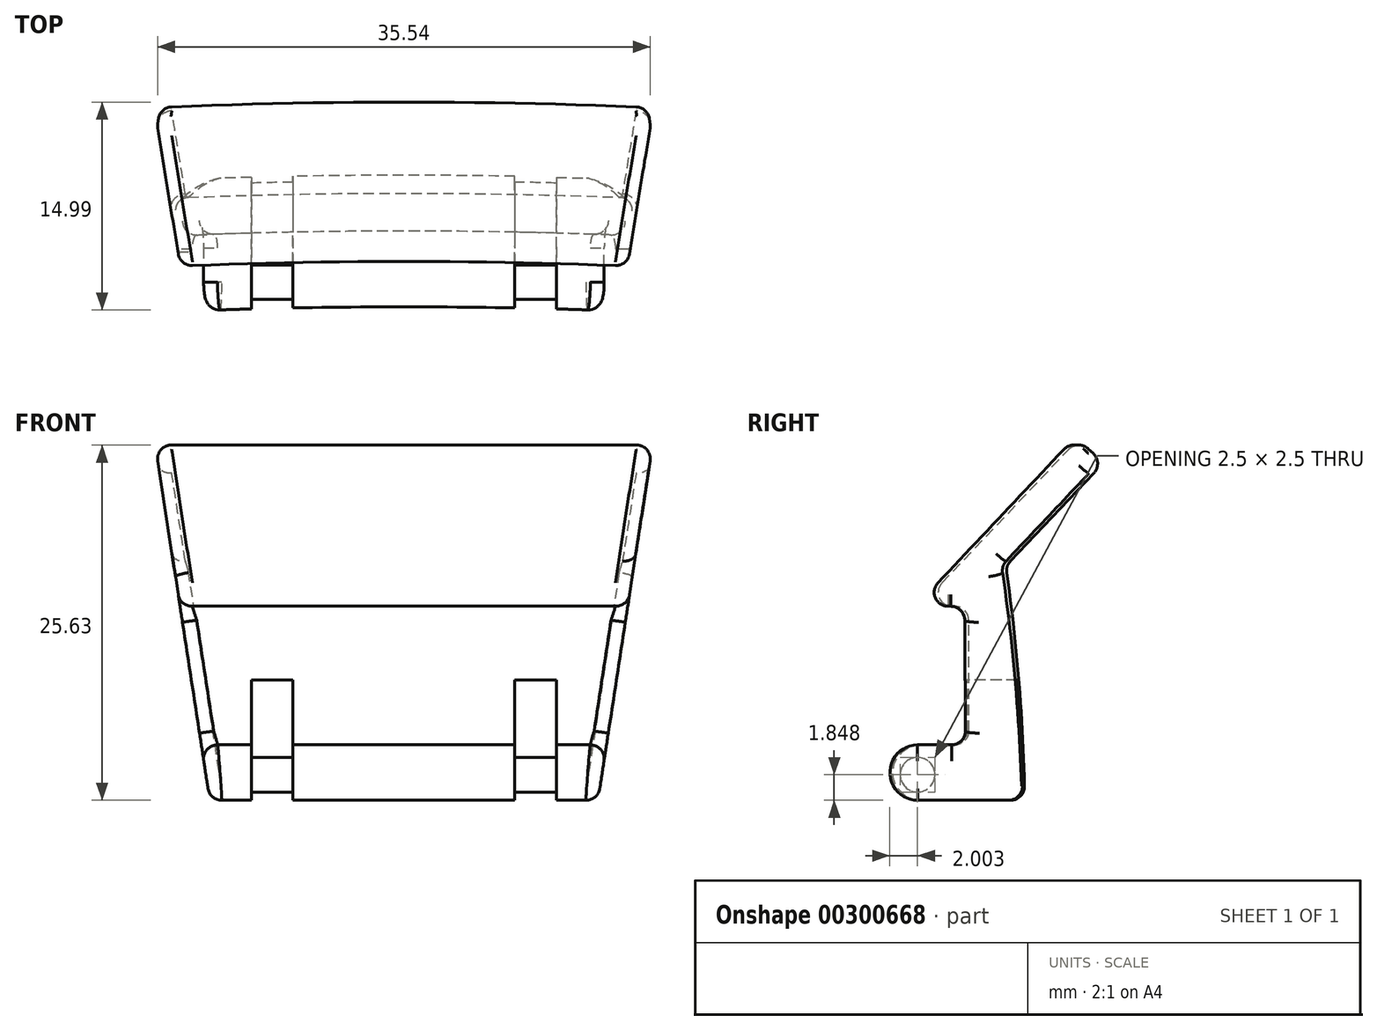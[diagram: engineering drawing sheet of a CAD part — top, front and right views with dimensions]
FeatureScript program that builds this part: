
annotation { "Feature Type Name" : "Feature", "Feature Type Description" : "" }
export const myFeature = defineFeature(function(context is Context, id is Id, definition is map)
    precondition{}
    {
        {
            var Q0;
            Q0=qCreatedBy(makeId("Right.planeOp"),FACE);
            var sketch = newSketch(context, id + "F0", { "sketchPlane" : qUnion([Q0])});
            skLineSegment(sketch, "E0", {"start": v(0, 14) * mm, "end": v(-3.52, 14) * mm});
            skLineSegment(sketch, "E1", {"start": v(-3.52, 14) * mm, "end": v(7.9, 26.05) * mm});
            skArc(sketch, "E2", {"start": v(4.05, 0) * mm, "mid": v(3.63, 8.47) * mm, "end": v(2.68, 16.9) * mm});
            skLineSegment(sketch, "E3", {"start": v(0, 14) * mm, "end": v(0, 4) * mm});
            skLineSegment(sketch, "E4", {"start": v(0, 4) * mm, "end": v(-3.46, 4) * mm});
            skLineSegment(sketch, "E5", {"start": v(-3.46, 0) * mm, "end": v(4.05, 0) * mm});
            skArc(sketch, "E6", {"start": v(-3.46, 4) * mm, "mid": v(-5.46, 2) * mm, "end": v(-3.46, 0) * mm});
            skLineSegment(sketch, "E7", {"start": v(-400, 131.7) * mm, "end": v(-400, -58.06) * mm, "construction": true});
            skPoint(sketch, "E8", {"position": v(2.2, 25.83) * mm});
            skLineSegment(sketch, "E9", {"start": v(7.9, 26.05) * mm, "end": v(9.72, 24.33) * mm});
            skLineSegment(sketch, "E10.trimOffspring", {"start": v(2.68, 16.9) * mm, "end": v(9.72, 24.33) * mm});
            skPoint(sketch, "E11.orphan", {"position": v(2.2, 20.02) * mm});
            skSolve(sketch);
        }
        {
            var Q0;
            Q0 = qSketchRegion(id + "F0", true);
            var Q1;
            Q1=sQuery(id+"F0.wireOp",EDGE,"E7");
            revolve(context, id + "F1", {"entities" : qUnion([Q0]), "axis" : qUnion([Q1]), "revolveType" : RevolveType.SYMMETRIC, "angle" : 10 * degree});
        }
        {
            var Q0;
            Q0=qCreatedBy(makeId("Front.planeOp"),FACE);
            var sketch = newSketch(context, id + "F2", { "sketchPlane" : qUnion([Q0])});
            skLineSegment(sketch, "E12", {"start": v(-14, 0) * mm, "end": v(-18, 26.05) * mm});
            skLineSegment(sketch, "E13", {"start": v(0, -20.72) * mm, "end": v(0, 33) * mm, "construction": true});
            skLineSegment(sketch, "E14", {"start": v(-11, -2.73) * mm, "end": v(-11, 8.67) * mm});
            skLineSegment(sketch, "E15", {"start": v(-11, 8.67) * mm, "end": v(-8, 8.67) * mm});
            skLineSegment(sketch, "E16", {"start": v(-8, 8.67) * mm, "end": v(-8, -4.43) * mm});
            skLineSegment(sketch, "E17", {"start": v(-11, -2.73) * mm, "end": v(-14, 0) * mm});
            skLineSegment(sketch, "E18", {"start": v(-8, -4.43) * mm, "end": v(0, -4.43) * mm});
            skPoint(sketch, "E18.endSnap0", {"position": v(0, 6.14) * mm});
            skLineSegment(sketch, "E19", {"start": v(-18, 26.05) * mm, "end": v(-24.18, 31.48) * mm});
            skLineSegment(sketch, "E20", {"start": v(-24.18, 31.48) * mm, "end": v(-48.84, 27.93) * mm});
            skLineSegment(sketch, "E21", {"start": v(-48.84, 27.93) * mm, "end": v(-46.83, -19.22) * mm});
            skLineSegment(sketch, "E22", {"start": v(-46.83, -19.22) * mm, "end": v(0, -26.62) * mm});
            skLineSegment(sketch, "E23.MirrorCS", {"start": v(46.83, -19.22) * mm, "end": v(0, -26.62) * mm});
            skLineSegment(sketch, "E24.MirrorCS", {"start": v(48.84, 27.93) * mm, "end": v(46.83, -19.22) * mm});
            skLineSegment(sketch, "E25.MirrorCS", {"start": v(24.18, 31.48) * mm, "end": v(48.84, 27.93) * mm});
            skLineSegment(sketch, "E26.MirrorCS", {"start": v(18, 26.05) * mm, "end": v(24.18, 31.48) * mm});
            skLineSegment(sketch, "E27.MirrorCS", {"start": v(14, 0) * mm, "end": v(18, 26.05) * mm});
            skLineSegment(sketch, "E28.MirrorCS", {"start": v(11, -2.73) * mm, "end": v(14, 0) * mm});
            skLineSegment(sketch, "E29.MirrorCS", {"start": v(11, -2.73) * mm, "end": v(11, 8.67) * mm});
            skLineSegment(sketch, "E30.MirrorCS", {"start": v(11, 8.67) * mm, "end": v(8, 8.67) * mm});
            skLineSegment(sketch, "E31.MirrorCS", {"start": v(8, 8.67) * mm, "end": v(8, -4.43) * mm});
            skLineSegment(sketch, "E32.MirrorCS", {"start": v(8, -4.43) * mm, "end": v(0, -4.43) * mm});
            skSolve(sketch);
        }
        {
            var Q0;
            Q0 = qSketchRegion(id + "F2", true);
            extrude(context, id + "F3", {"entities" : qUnion([Q0]), "operationType" : NewBodyOperationType.REMOVE, "oppositeDirection" : true, "depth" : 19.2 * mm, "hasSecondDirection" : true, "secondDirectionOppositeDirection" : false, "secondDirectionDepth" : 25 * mm});
        }
        {
            var Q0;
            Q0=makeQuery(id+"F1.opRevolve","SWEPT_EDGE",EDGE,{"disambiguationData":[OSD([sQuery(id+"F0.wireOp",EDGE,"E0"),sQuery(id+"F0.wireOp",EDGE,"E1")])]});
            var Q1;
            Q1=makeQuery(id+"F1.opRevolve","SWEPT_EDGE",EDGE,{"disambiguationData":[OSD([sQuery(id+"F0.wireOp",EDGE,"E0"),sQuery(id+"F0.wireOp",EDGE,"E3")])]});
            var Q2;
            {var subQ0=sQuery(id+"F0.wireOp",EDGE,"E3");var subQ1=sQuery(id+"F0.wireOp",EDGE,"E4");Q2=makeQuery(id+"F3.boolean.opBoolean","SPLIT",EDGE,{"disambiguationData":[TD([makeQuery(id+"F3.opExtrude","SWEPT_FACE",FACE,{"disambiguationData":[OSD([sQuery(id+"F2.wireOp",EDGE,"E27.MirrorCS")])]})])],"derivedFrom":makeQuery(id+"F1.opRevolve","SWEPT_EDGE",EDGE,{"disambiguationData":[OSD([subQ0,subQ1])]})});}
            var Q3;
            {var subQ0=sQuery(id+"F0.wireOp",EDGE,"E3");var subQ1=sQuery(id+"F0.wireOp",EDGE,"E4");Q3=makeQuery(id+"F3.boolean.opBoolean","SPLIT",EDGE,{"disambiguationData":[TD([makeQuery(id+"F3.opExtrude","SWEPT_FACE",FACE,{"disambiguationData":[OSD([sQuery(id+"F2.wireOp",EDGE,"E16")])]})])],"derivedFrom":makeQuery(id+"F1.opRevolve","SWEPT_EDGE",EDGE,{"disambiguationData":[OSD([subQ0,subQ1])]})});}
            var Q4;
            {var subQ0=sQuery(id+"F0.wireOp",EDGE,"E3");var subQ1=sQuery(id+"F0.wireOp",EDGE,"E4");Q4=makeQuery(id+"F3.boolean.opBoolean","SPLIT",EDGE,{"disambiguationData":[TD([makeQuery(id+"F3.opExtrude","SWEPT_FACE",FACE,{"disambiguationData":[OSD([sQuery(id+"F2.wireOp",EDGE,"E12")])]})])],"derivedFrom":makeQuery(id+"F1.opRevolve","SWEPT_EDGE",EDGE,{"disambiguationData":[OSD([subQ0,subQ1])]})});}
            var Q5;
            {var subQ0=sQuery(id+"F0.wireOp",EDGE,"E2");var subQ1=sQuery(id+"F0.wireOp",EDGE,"E5");Q5=makeQuery(id+"F3.boolean.opBoolean","SPLIT",EDGE,{"disambiguationData":[TD([makeQuery(id+"F3.opExtrude","SWEPT_FACE",FACE,{"disambiguationData":[OSD([sQuery(id+"F2.wireOp",EDGE,"E16")])]})])],"derivedFrom":makeQuery(id+"F1.opRevolve","SWEPT_EDGE",EDGE,{"disambiguationData":[OSD([subQ0,subQ1])]})});}
            var Q6;
            {var subQ0=sQuery(id+"F0.wireOp",EDGE,"E2");var subQ1=sQuery(id+"F0.wireOp",EDGE,"E5");Q6=makeQuery(id+"F3.boolean.opBoolean","SPLIT",EDGE,{"disambiguationData":[TD([makeQuery(id+"F3.opExtrude","SWEPT_FACE",FACE,{"disambiguationData":[OSD([sQuery(id+"F2.wireOp",EDGE,"E27.MirrorCS")])]})])],"derivedFrom":makeQuery(id+"F1.opRevolve","SWEPT_EDGE",EDGE,{"disambiguationData":[OSD([subQ0,subQ1])]})});}
            var Q7;
            Q7=makeQuery(id+"F1.opRevolve","SWEPT_EDGE",EDGE,{"disambiguationData":[OSD([sQuery(id+"F0.wireOp",EDGE,"E2"),sQuery(id+"F0.wireOp",EDGE,"E10.trimOffspring")])]});
            var Q8;
            {var subQ0=sQuery(id+"F0.wireOp",EDGE,"E2");var subQ1=sQuery(id+"F0.wireOp",EDGE,"E5");Q8=makeQuery(id+"F3.boolean.opBoolean","SPLIT",EDGE,{"disambiguationData":[TD([makeQuery(id+"F3.opExtrude","SWEPT_FACE",FACE,{"disambiguationData":[OSD([sQuery(id+"F2.wireOp",EDGE,"E12")])]})])],"derivedFrom":makeQuery(id+"F1.opRevolve","SWEPT_EDGE",EDGE,{"disambiguationData":[OSD([subQ0,subQ1])]})});}
            var Q9;
            Q9=makeQuery(id+"F1.opRevolve","SWEPT_EDGE",EDGE,{"disambiguationData":[OSD([sQuery(id+"F0.wireOp",EDGE,"E1"),sQuery(id+"F0.wireOp",EDGE,"E9")])]});
            var Q10;
            Q10=makeQuery(id+"F1.opRevolve","SWEPT_EDGE",EDGE,{"disambiguationData":[OSD([sQuery(id+"F0.wireOp",EDGE,"E9"),sQuery(id+"F0.wireOp",EDGE,"E10.trimOffspring")])]});
            var Q11;
            Q11=makeQuery(id+"F3.boolean.opBoolean","COPY",FACE,{"derivedFrom":makeQuery(id+"F3.opExtrude","SWEPT_FACE",FACE,{"disambiguationData":[OSD([sQuery(id+"F2.wireOp",EDGE,"E27.MirrorCS")])]})});
            var Q12;
            Q12=makeQuery(id+"F3.boolean.opBoolean","INTERSECT",EDGE,{"derivedFrom":[makeQuery(id+"F1.opRevolve","SWEPT_FACE",FACE,{"disambiguationData":[OSD([sQuery(id+"F0.wireOp",EDGE,"E3")])]}),makeQuery(id+"F3.opExtrude","SWEPT_FACE",FACE,{"disambiguationData":[OSD([sQuery(id+"F2.wireOp",EDGE,"E12")])]})]});
            var Q13;
            Q13=makeQuery(id+"F3.boolean.opBoolean","COPY",FACE,{"derivedFrom":makeQuery(id+"F3.opExtrude","SWEPT_FACE",FACE,{"disambiguationData":[OSD([sQuery(id+"F2.wireOp",EDGE,"E12")])]})});
            fillet(context, id + "F4", {"entities" : qUnion([Q0, Q1, Q2, Q3, Q4, Q5, Q6, Q7, Q8, Q9, Q10, Q11, Q12, Q13]), "radius" : 1 * mm, "tangentPropagation" : true, "allowEdgeOverflow" : false});
        }
        {
            var Q0;
            Q0=qCreatedBy(makeId("Right.planeOp"),FACE);
            var sketch = newSketch(context, id + "F5", { "sketchPlane" : qUnion([Q0])});
            skLineSegment(sketch, "E33", {"start": v(-3.68, 0.85) * mm, "end": v(-3.7, 2.85) * mm, "construction": true});
            skCircle(sketch, "E34", {"center": v(-3.69, 1.85) * mm, "radius": 1.25 * mm});
            skSolve(sketch);
        }
        {
            var Q0;
            Q0 = qSketchRegion(id + "F5", true);
            extrude(context, id + "F6", {"entities" : qUnion([Q0]), "operationType" : NewBodyOperationType.ADD, "endBound" : BoundingType.SYMMETRIC, "depth" : 23 * mm});
        }
    });
